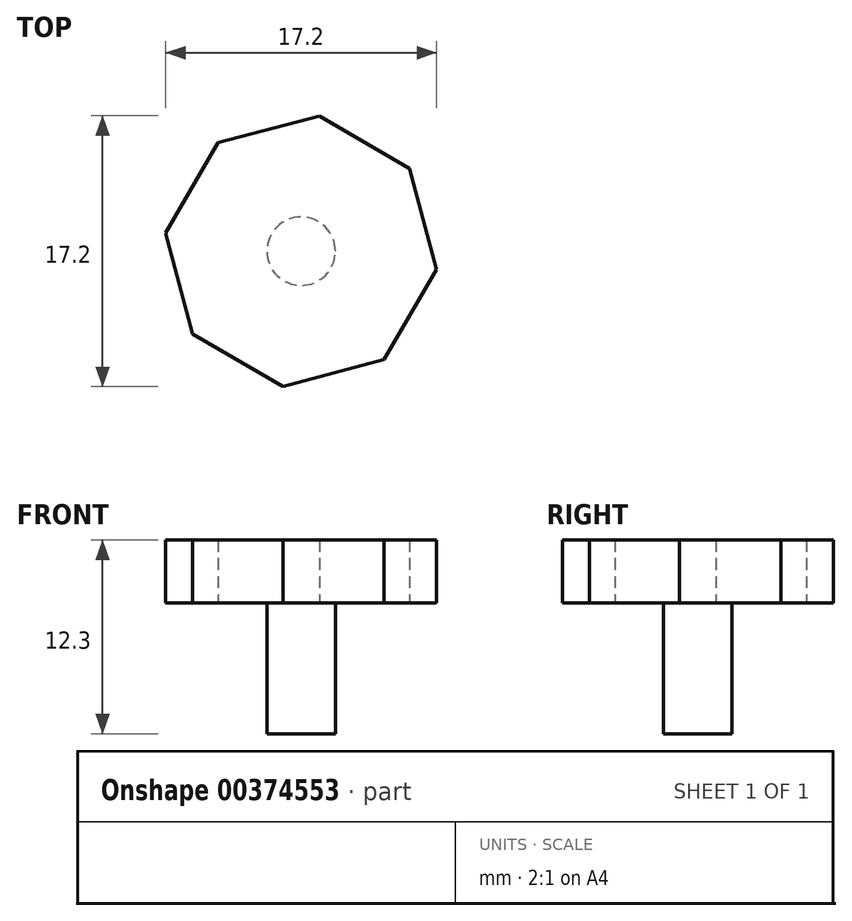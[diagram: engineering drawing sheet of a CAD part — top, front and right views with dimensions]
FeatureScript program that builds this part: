
annotation { "Feature Type Name" : "Feature", "Feature Type Description" : "" }
export const myFeature = defineFeature(function(context is Context, id is Id, definition is map)
    precondition{}
    {
        {
            var Q0;
            Q0=qCreatedBy(makeId("Top.planeOp"),FACE);
            var sketch = newSketch(context, id + "F0", { "sketchPlane" : qUnion([Q0])});
            skCircle(sketch, "E0", {"center": v(0, 0) * mm, "radius": 2.17 * mm});
            skSolve(sketch);
        }
        {
            var Q0;
            Q0 = qSketchRegion(id + "F0", true);
            extrude(context, id + "F1", {"entities" : qUnion([Q0]), "depth" : 8.3 * mm});
        }
        {
            var Q0;
            Q0=makeQuery(id+"F1.opExtrude","CAP_FACE",FACE,{"disambiguationData":[OSD([sQuery(id+"F0.wireOp",EDGE,"E0")])],"isStart":false});
            var sketch = newSketch(context, id + "F2", { "sketchPlane" : qUnion([Q0])});
            skCircle(sketch, "E1.cCircle", {"center": v(0, 0) * mm, "radius": 8.01 * mm, "construction": true});
            skLineSegment(sketch, "E1.0", {"start": v(8.6, -1.16) * mm, "end": v(5.26, -6.9) * mm});
            skLineSegment(sketch, "E1.1", {"start": v(5.26, -6.9) * mm, "end": v(-1.16, -8.6) * mm});
            skLineSegment(sketch, "E1.2", {"start": v(-1.16, -8.6) * mm, "end": v(-6.9, -5.26) * mm});
            skLineSegment(sketch, "E1.3", {"start": v(-6.9, -5.26) * mm, "end": v(-8.6, 1.16) * mm});
            skLineSegment(sketch, "E1.4", {"start": v(-8.6, 1.16) * mm, "end": v(-5.26, 6.9) * mm});
            skLineSegment(sketch, "E1.5", {"start": v(-5.26, 6.9) * mm, "end": v(1.16, 8.6) * mm});
            skLineSegment(sketch, "E1.6", {"start": v(1.16, 8.6) * mm, "end": v(6.9, 5.26) * mm});
            skLineSegment(sketch, "E1.7", {"start": v(6.9, 5.26) * mm, "end": v(8.6, -1.16) * mm});
            skPoint(sketch, "E1.0.midPoint", {"position": v(6.93, -4.03) * mm});
            skSolve(sketch);
        }
        {
            var Q0;
            Q0=makeQuery(id+"F2.imprint","IMPRINT",FACE,{"disambiguationData":[TD([[makeQuery(id+"F2.imprint","IMPRINT",EDGE,{"derivedFrom":sQuery(id+"F2.wireOp",EDGE,"E1.0")}),-1.0]])]});
            var Q1;
            Q1=makeQuery(id+"F2.imprint","IMPRINT",FACE,{"disambiguationData":[TD([[makeQuery(id+"F2.imprint","IMPRINT",EDGE,{"derivedFrom":makeQuery(id+"F1.opExtrude","CAP_EDGE",EDGE,{"disambiguationData":[OSD([sQuery(id+"F0.wireOp",EDGE,"E0")])],"isStart":false})}),1.0]])]});
            extrude(context, id + "F3", {"entities" : qUnion([Q0, Q1]), "operationType" : NewBodyOperationType.ADD, "depth" : 4 * mm});
        }
    });
